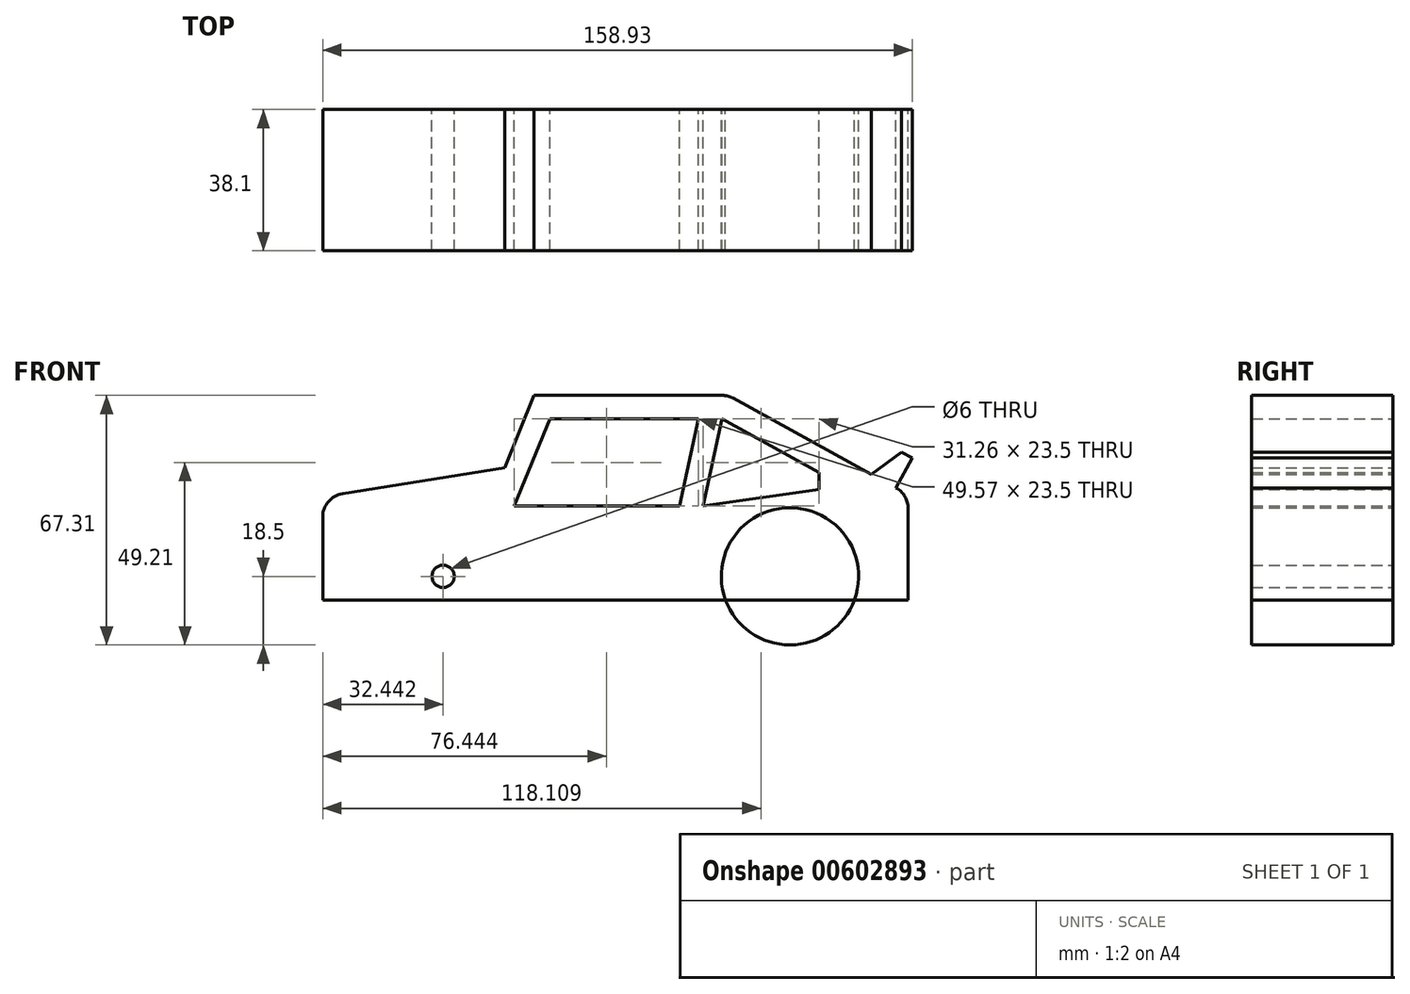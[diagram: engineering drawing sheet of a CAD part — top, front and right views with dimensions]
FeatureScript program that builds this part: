
annotation { "Feature Type Name" : "Feature", "Feature Type Description" : "" }
export const myFeature = defineFeature(function(context is Context, id is Id, definition is map)
    precondition{}
    {
        {
            var Q0;
            Q0=qCreatedBy(makeId("Front.planeOp"),FACE);
            var sketch = newSketch(context, id + "F0", { "sketchPlane" : qUnion([Q0])});
            skCircle(sketch, "E0", {"center": v(-46.46, 0) * mm, "radius": 18.5 * mm});
            skCircle(sketch, "E1", {"center": v(47.03, 0) * mm, "radius": 18.5 * mm});
            skLineSegment(sketch, "E2.bottom", {"start": v(78.9, -6.35) * mm, "end": v(-78.9, -6.35) * mm});
            skPoint(sketch, "E2.middle", {"position": v(0, 0) * mm});
            skLineSegment(sketch, "E3", {"start": v(-73.56, 22.27) * mm, "end": v(-29.88, 29.31) * mm});
            skLineSegment(sketch, "E4", {"start": v(-29.88, 29.31) * mm, "end": v(-21.92, 48.81) * mm});
            skLineSegment(sketch, "E5", {"start": v(-21.92, 48.81) * mm, "end": v(28.68, 48.81) * mm});
            skLineSegment(sketch, "E6", {"start": v(31.74, 48.02) * mm, "end": v(68.97, 27.54) * mm});
            skLineSegment(sketch, "E7", {"start": v(78.9, 18.32) * mm, "end": v(78.9, -6.35) * mm});
            skLineSegment(sketch, "E8", {"start": v(-78.9, 16) * mm, "end": v(-78.9, -6.35) * mm});
            skLineSegment(sketch, "E9.0", {"start": v(28.68, 42.46) * mm, "end": v(54.84, 28.07) * mm});
            skLineSegment(sketch, "E9.1", {"start": v(-17.65, 42.46) * mm, "end": v(22.33, 42.46) * mm});
            skPoint(sketch, "E10.visualSharp", {"position": v(78.9, 22.07) * mm});
            skArc(sketch, "E10.filletArc", {"start": v(78.9, 18.32) * mm, "mid": v(78.02, 21.55) * mm, "end": v(75.61, 23.88) * mm});
            skPoint(sketch, "E11.visualSharp", {"position": v(-78.9, 21.41) * mm});
            skArc(sketch, "E11.filletArc", {"start": v(-73.56, 22.27) * mm, "mid": v(-77.39, 20.12) * mm, "end": v(-78.9, 16) * mm});
            skPoint(sketch, "E12.visualSharp", {"position": v(30.3, 48.81) * mm});
            skArc(sketch, "E12.filletArc", {"start": v(31.74, 48.02) * mm, "mid": v(30.26, 48.61) * mm, "end": v(28.68, 48.81) * mm});
            skLineSegment(sketch, "E13", {"start": v(75.61, 23.88) * mm, "end": v(80.03, 31.91) * mm});
            skLineSegment(sketch, "E14", {"start": v(80.03, 31.91) * mm, "end": v(77.13, 33.51) * mm});
            skLineSegment(sketch, "E15", {"start": v(68.97, 27.54) * mm, "end": v(77.13, 33.51) * mm});
            skCircle(sketch, "E16", {"center": v(47.03, 0) * mm, "radius": 3 * mm});
            skCircle(sketch, "E17", {"center": v(-46.46, 0) * mm, "radius": 3 * mm});
            skLineSegment(sketch, "E18", {"start": v(28.68, 42.46) * mm, "end": v(23.58, 18.96) * mm});
            skLineSegment(sketch, "E19", {"start": v(22.33, 42.46) * mm, "end": v(17.23, 18.96) * mm});
            skLineSegment(sketch, "E20", {"start": v(-27.24, 18.96) * mm, "end": v(17.23, 18.96) * mm});
            skLineSegment(sketch, "E21", {"start": v(-17.65, 42.46) * mm, "end": v(-27.24, 18.96) * mm});
            skLineSegment(sketch, "E22", {"start": v(23.58, 18.96) * mm, "end": v(54.84, 23.48) * mm});
            skLineSegment(sketch, "E23", {"start": v(54.84, 23.48) * mm, "end": v(54.84, 28.07) * mm});
            skSolve(sketch);
        }
        {
            var Q0;
            Q0=makeQuery(id+"F0.imprint","IMPRINT",FACE,{"disambiguationData":[TD([[makeQuery(id+"F0.imprint","IMPRINT",EDGE,{"derivedFrom":sQuery(id+"F0.wireOp",EDGE,"E2.bottom")}),-1.0]])]});
            var Q1;
            {var subQ0=sQuery(id+"F0.wireOp",EDGE,"E2.bottom");var subQ1=sQuery(id+"F0.wireOp",EDGE,"E0");var subQ2=makeQuery(id+"F0.imprint","INTERSECT",VERTEX,{"disambiguationData":[OD(0.0)],"derivedFrom":[subQ1,subQ0]});Q1=makeQuery(id+"F0.imprint","IMPRINT",FACE,{"disambiguationData":[TD([[makeQuery(id+"F0.imprint","IMPRINT",EDGE,{"disambiguationData":[TD([[subQ2,-1.0]])],"derivedFrom":subQ1}),1.0]])]});}
            var Q2;
            {var subQ0=sQuery(id+"F0.wireOp",EDGE,"E2.bottom");var subQ1=sQuery(id+"F0.wireOp",EDGE,"E1");var subQ2=makeQuery(id+"F0.imprint","INTERSECT",VERTEX,{"disambiguationData":[OD(0.0)],"derivedFrom":[subQ1,subQ0]});Q2=makeQuery(id+"F0.imprint","IMPRINT",FACE,{"disambiguationData":[TD([[makeQuery(id+"F0.imprint","IMPRINT",EDGE,{"disambiguationData":[TD([[subQ2,-1.0]])],"derivedFrom":subQ1}),1.0]])]});}
            extrude(context, id + "F1", {"entities" : qUnion([Q0, Q1, Q2]), "depth" : 38.1 * mm, "offsetDistance" : 25.4 * mm});
        }
    });
